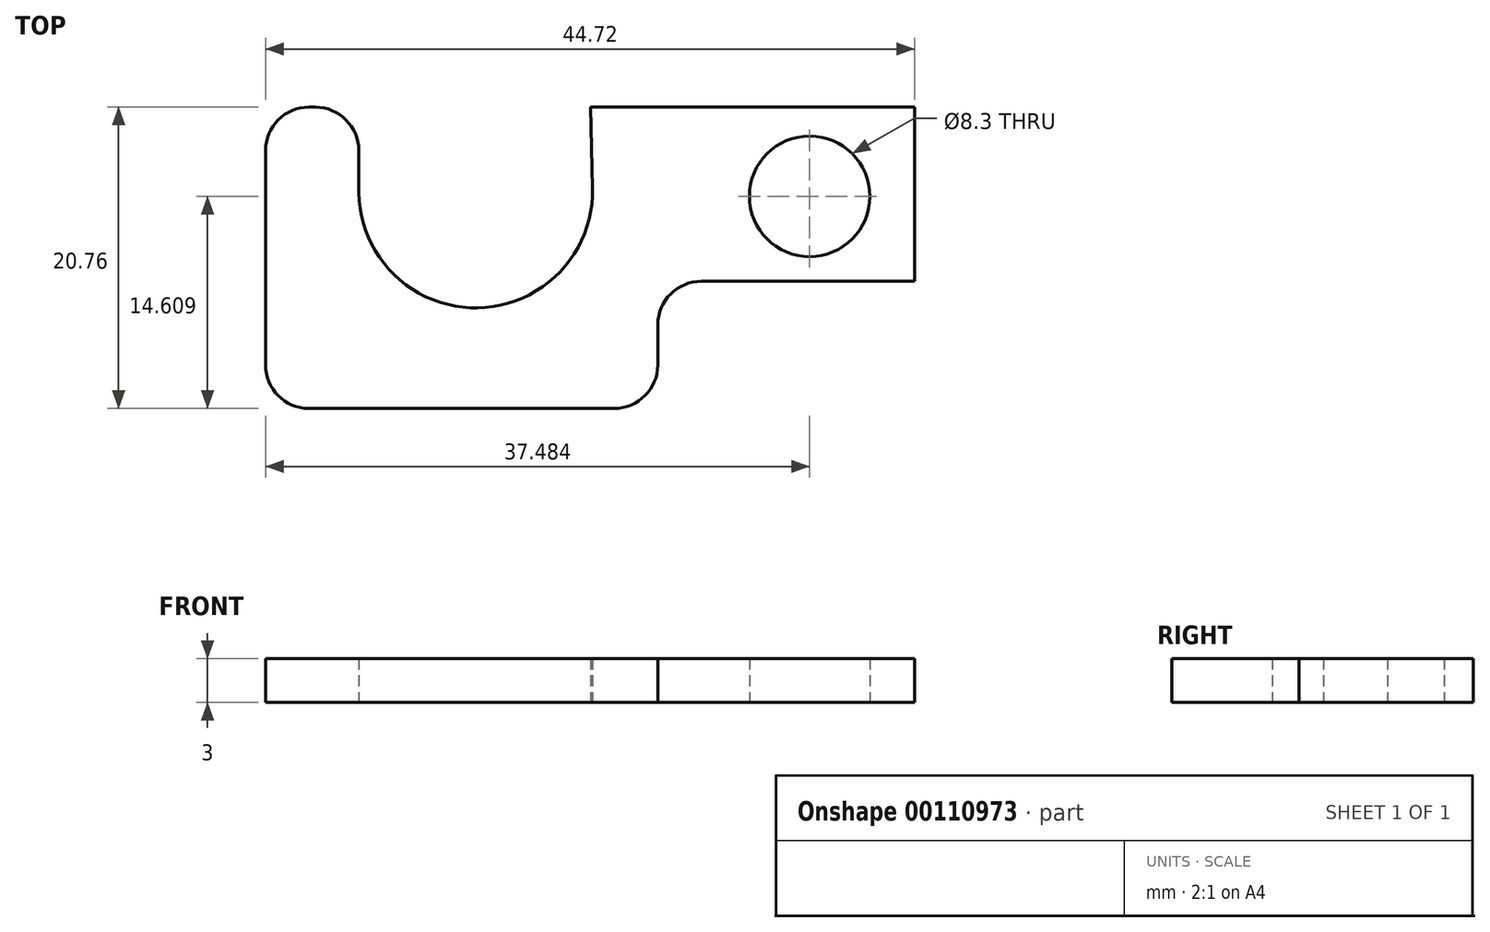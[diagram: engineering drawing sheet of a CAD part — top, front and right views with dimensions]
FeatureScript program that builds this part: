
annotation { "Feature Type Name" : "Feature", "Feature Type Description" : "" }
export const myFeature = defineFeature(function(context is Context, id is Id, definition is map)
    precondition{}
    {
        {
            var Q0;
            Q0=qCreatedBy(makeId("Top.planeOp"),FACE);
            var sketch = newSketch(context, id + "F0", { "sketchPlane" : qUnion([Q0])});
            skLineSegment(sketch, "E0", {"start": v(31.97, 8) * mm, "end": v(9.66, 8) * mm});
            skLineSegment(sketch, "E1", {"start": v(-12.75, 5) * mm, "end": v(-12.75, -9.75) * mm});
            skLineSegment(sketch, "E2", {"start": v(-9.75, -12.75) * mm, "end": v(11.27, -12.75) * mm});
            skLineSegment(sketch, "E3", {"start": v(14.27, -9.75) * mm, "end": v(14.27, -7) * mm});
            skLineSegment(sketch, "E4", {"start": v(17.27, -4) * mm, "end": v(31.97, -4) * mm});
            skLineSegment(sketch, "E5", {"start": v(31.97, -4) * mm, "end": v(31.97, 8) * mm});
            skArc(sketch, "E6", {"start": v(-6.33, 2.34) * mm, "mid": v(1.75, -5.83) * mm, "end": v(9.77, 2.4) * mm});
            skLineSegment(sketch, "E7", {"start": v(-6.33, 2.11) * mm, "end": v(-6.33, 5) * mm});
            skLineSegment(sketch, "E8", {"start": v(9.77, 2.4) * mm, "end": v(9.66, 8) * mm});
            skLineSegment(sketch, "E9.trimOffspring", {"start": v(-9.33, 8) * mm, "end": v(-9.75, 8) * mm});
            skCircle(sketch, "E10", {"center": v(24.73, 1.86) * mm, "radius": 4.15 * mm});
            skPoint(sketch, "E11.visualSharp", {"position": v(14.27, -4) * mm});
            skArc(sketch, "E11.filletArc", {"start": v(17.27, -4) * mm, "mid": v(15.15, -4.87) * mm, "end": v(14.27, -7) * mm});
            skPoint(sketch, "E12.visualSharp", {"position": v(-12.75, -12.75) * mm});
            skArc(sketch, "E12.filletArc", {"start": v(-12.75, -9.75) * mm, "mid": v(-11.88, -11.88) * mm, "end": v(-9.75, -12.75) * mm});
            skPoint(sketch, "E13.visualSharp", {"position": v(14.27, -12.75) * mm});
            skArc(sketch, "E13.filletArc", {"start": v(11.27, -12.75) * mm, "mid": v(13.4, -11.88) * mm, "end": v(14.27, -9.75) * mm});
            skPoint(sketch, "E14.visualSharp", {"position": v(-12.75, 8) * mm});
            skArc(sketch, "E14.filletArc", {"start": v(-9.75, 8) * mm, "mid": v(-11.88, 7.13) * mm, "end": v(-12.75, 5) * mm});
            skPoint(sketch, "E15.visualSharp", {"position": v(-6.33, 8) * mm});
            skArc(sketch, "E15.filletArc", {"start": v(-6.33, 5) * mm, "mid": v(-7.2, 7.13) * mm, "end": v(-9.33, 8) * mm});
            skSolve(sketch);
        }
        {
            var Q0;
            Q0 = qSketchRegion(id + "F0", true);
            extrude(context, id + "F1", {"entities" : qUnion([Q0]), "depth" : 3 * mm});
        }
    });
